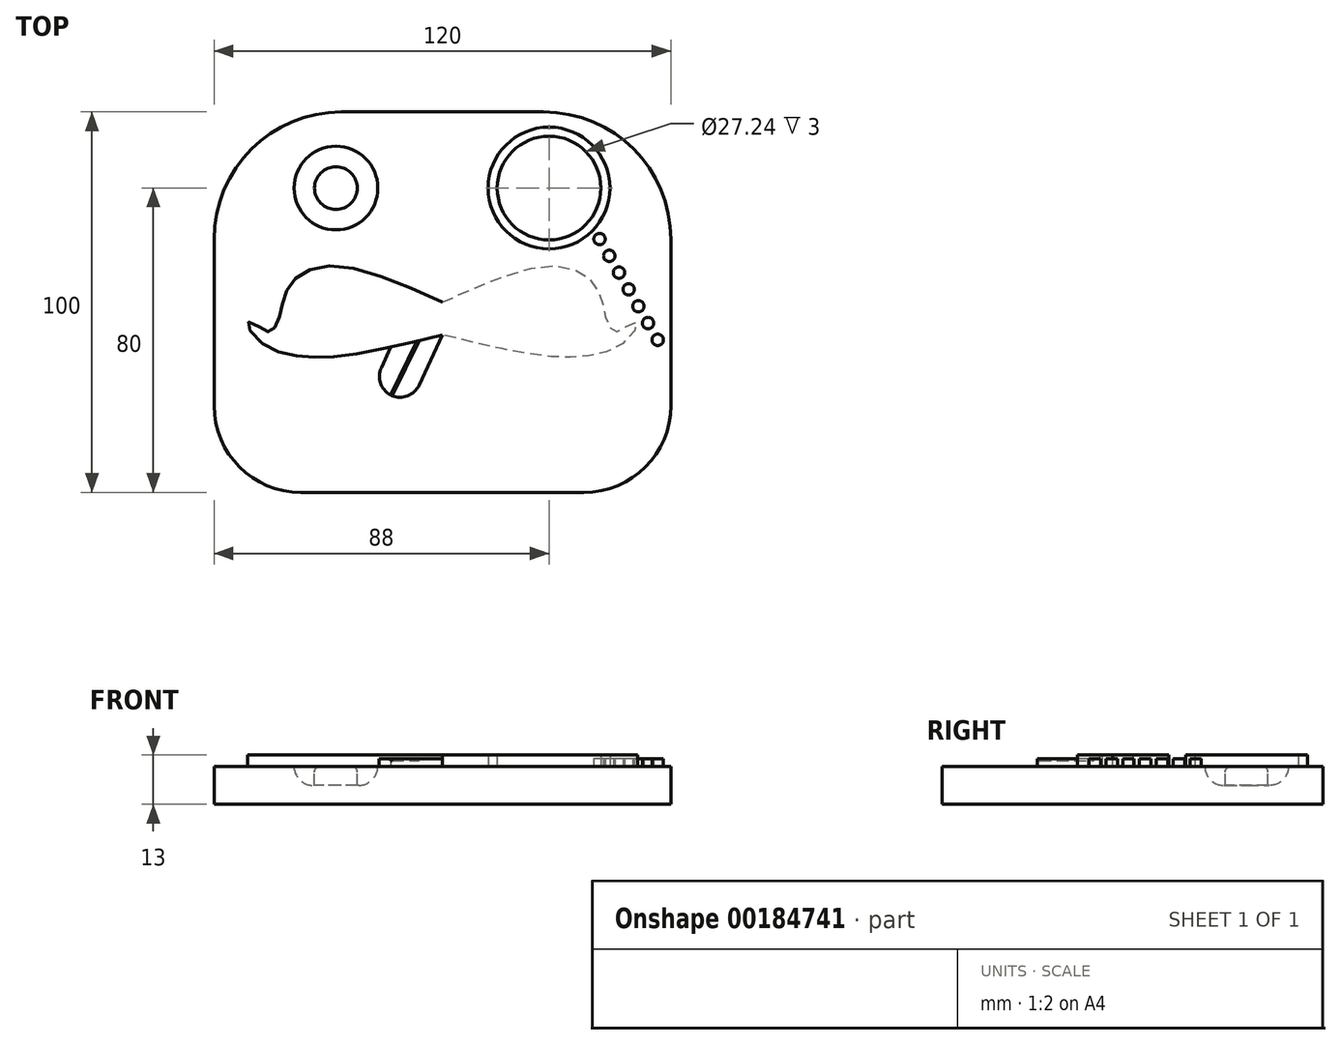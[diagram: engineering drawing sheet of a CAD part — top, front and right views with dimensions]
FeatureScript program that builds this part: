
annotation { "Feature Type Name" : "Feature", "Feature Type Description" : "" }
export const myFeature = defineFeature(function(context is Context, id is Id, definition is map)
    precondition{}
    {
        {
            var Q0;
            Q0=qCreatedBy(makeId("Top.planeOp"),FACE);
            var sketch = newSketch(context, id + "F0", { "sketchPlane" : qUnion([Q0])});
            skLineSegment(sketch, "E0.bottom", {"start": v(37.2, -50) * mm, "end": v(-37.2, -50) * mm});
            skLineSegment(sketch, "E0.top", {"start": v(26.57, 50) * mm, "end": v(-26.57, 50) * mm});
            skLineSegment(sketch, "E0.left", {"start": v(60, -27.2) * mm, "end": v(60, 16.57) * mm});
            skLineSegment(sketch, "E0.right", {"start": v(-60, -27.2) * mm, "end": v(-60, 16.57) * mm});
            skPoint(sketch, "E0.middle", {"position": v(0, 0) * mm});
            skPoint(sketch, "E1.visualSharp", {"position": v(-60, 50) * mm});
            skArc(sketch, "E1.filletArc", {"start": v(-26.57, 50) * mm, "mid": v(-50.2, 40.2) * mm, "end": v(-60, 16.57) * mm});
            skPoint(sketch, "E2.visualSharp", {"position": v(60, 50) * mm});
            skArc(sketch, "E2.filletArc", {"start": v(60, 16.57) * mm, "mid": v(50.2, 40.2) * mm, "end": v(26.57, 50) * mm});
            skPoint(sketch, "E3.visualSharp", {"position": v(-60, -50) * mm});
            skArc(sketch, "E3.filletArc", {"start": v(-60, -27.2) * mm, "mid": v(-53.32, -43.32) * mm, "end": v(-37.2, -50) * mm});
            skPoint(sketch, "E4.visualSharp", {"position": v(60, -50) * mm});
            skArc(sketch, "E4.filletArc", {"start": v(37.2, -50) * mm, "mid": v(53.32, -43.32) * mm, "end": v(60, -27.2) * mm});
            skSolve(sketch);
        }
        {
            var Q0;
            Q0 = qSketchRegion(id + "F0", true);
            extrude(context, id + "F1", {"entities" : qUnion([Q0]), "depth" : 10 * mm});
        }
        {
            var Q0;
            Q0=makeQuery(id+"F1.opExtrude","CAP_FACE",FACE,{"disambiguationData":[OSD([sQuery(id+"F0.wireOp",EDGE,"E0.bottom"),sQuery(id+"F0.wireOp",EDGE,"E0.top"),sQuery(id+"F0.wireOp",EDGE,"E0.left"),sQuery(id+"F0.wireOp",EDGE,"E0.right"),sQuery(id+"F0.wireOp",EDGE,"E1.filletArc"),sQuery(id+"F0.wireOp",EDGE,"E2.filletArc"),sQuery(id+"F0.wireOp",EDGE,"E3.filletArc"),sQuery(id+"F0.wireOp",EDGE,"E4.filletArc")])],"isStart":false});
            cPlane(context, id + "F2", {"entities" : qUnion([Q0]), "cplaneType" : CPlaneType.OFFSET, "offset" : 0 * mm, "width" : 150 * mm, "height" : 150 * mm});
        }
        {
            var Q0;
            Q0=qCreatedBy(id+"F2.planeOp",FACE);
            var sketch = newSketch(context, id + "F3", { "sketchPlane" : qUnion([Q0])});
            skFitSpline(sketch, "E5", {"points": [v(0, 0) * mm, v(-28.4, 9.57) * mm, v(-38.75, 6) * mm, v(-41.96, 0) * mm, v(-43.27, -5.29) * mm, v(-45.4, -7.79) * mm, v(-47.3, -6.95) * mm, v(-51.11, -5.29) * mm, v(-48.14, -10.28) * mm, v(-38.28, -14.09) * mm, v(-26.03, -14.09) * mm, v(0, -8.62) * mm], "startDerivative": vector(-190.26, 85.43) * mm, "endDerivative": vector(183.95, 44.61) * mm});
            skLineSegment(sketch, "E6", {"start": v(0, 71.97) * mm, "end": v(0, -72.57) * mm, "construction": true});
            skFitSpline(sketch, "E7.MirrorCS", {"points": [v(0, 0) * mm, v(28.4, 9.57) * mm, v(38.75, 6) * mm, v(41.96, 0) * mm, v(43.27, -5.29) * mm, v(45.4, -7.79) * mm, v(47.3, -6.95) * mm, v(51.11, -5.29) * mm, v(48.14, -10.28) * mm, v(38.28, -14.09) * mm, v(26.03, -14.09) * mm, v(0, -8.62) * mm], "startDerivative": vector(190.26, 85.43) * mm, "endDerivative": vector(-183.95, 44.61) * mm});
            skSolve(sketch);
        }
        {
            var Q0;
            Q0 = qSketchRegion(id + "F3", true);
            extrude(context, id + "F4", {"entities" : qUnion([Q0]), "operationType" : NewBodyOperationType.ADD, "depth" : 3 * mm});
        }
        {
            var Q0;
            Q0=qCreatedBy(id+"F2.planeOp",FACE);
            var sketch = newSketch(context, id + "F5", { "sketchPlane" : qUnion([Q0])});
            skLineSegment(sketch, "E8.bottom", {"start": v(-9.75, -3.6) * mm, "end": v(0.16, -8.23) * mm});
            skLineSegment(sketch, "E8.left", {"start": v(-9.75, -3.6) * mm, "end": v(-16.09, -17.2) * mm});
            skLineSegment(sketch, "E8.right", {"start": v(0.16, -8.23) * mm, "end": v(-6.18, -21.82) * mm});
            skLineSegment(sketch, "E9", {"start": v(0, 74.11) * mm, "end": v(0, -72.57) * mm, "construction": true});
            skArc(sketch, "E10", {"start": v(-16.09, -17.2) * mm, "mid": v(-13.44, -24.47) * mm, "end": v(-6.18, -21.82) * mm});
            skSolve(sketch);
        }
        {
            var Q0;
            Q0 = qSketchRegion(id + "F5", true);
            extrude(context, id + "F6", {"entities" : qUnion([Q0]), "operationType" : NewBodyOperationType.ADD, "depth" : 2 * mm});
        }
        {
            var Q0;
            Q0=qCreatedBy(id+"F2.planeOp",FACE);
            var sketch = newSketch(context, id + "F7", { "sketchPlane" : qUnion([Q0])});
            skLineSegment(sketch, "E11", {"start": v(0, 80.6) * mm, "end": v(0, -78.54) * mm, "construction": true});
            skCircle(sketch, "E12", {"center": v(-28, 30) * mm, "radius": 11 * mm});
            skCircle(sketch, "E13", {"center": v(-28, 30) * mm, "radius": 5.62 * mm});
            skCircle(sketch, "E14.MirrorC", {"center": v(28, 30) * mm, "radius": 11 * mm});
            skCircle(sketch, "E15.MirrorC", {"center": v(28, 30) * mm, "radius": 5.62 * mm});
            skSolve(sketch);
        }
        {
            var Q0;
            Q0=makeQuery(id+"F7.imprint","IMPRINT",FACE,{"disambiguationData":[TD([[makeQuery(id+"F7.imprint","IMPRINT",EDGE,{"derivedFrom":sQuery(id+"F7.wireOp",EDGE,"E12")}),1.0]])]});
            var Q1;
            Q1=makeQuery(id+"F7.imprint","IMPRINT",FACE,{"disambiguationData":[TD([[makeQuery(id+"F7.imprint","IMPRINT",EDGE,{"derivedFrom":sQuery(id+"F7.wireOp",EDGE,"E14.MirrorC")}),-1.0]])]});
            var Q2;
            Q2=sQuery(id+"F7.wireOp",EDGE,"E12");
            extrude(context, id + "F8", {"entities" : qUnion([Q0, Q1]), "operationType" : NewBodyOperationType.REMOVE, "surfaceEntities" : qUnion([Q2]), "oppositeDirection" : true, "depth" : 5 * mm});
        }
        {
            var Q0;
            Q0=makeQuery(id+"F8.boolean.opBoolean","COPY",EDGE,{"derivedFrom":makeQuery(id+"F8.opExtrude","CAP_EDGE",EDGE,{"disambiguationData":[OSD([sQuery(id+"F7.wireOp",EDGE,"E12")])],"isStart":false})});
            var Q1;
            Q1=makeQuery(id+"F8.boolean.opBoolean","COPY",EDGE,{"derivedFrom":makeQuery(id+"F8.opExtrude","CAP_EDGE",EDGE,{"disambiguationData":[OSD([sQuery(id+"F7.wireOp",EDGE,"E14.MirrorC")])],"isStart":false})});
            fillet(context, id + "F9", {"entities" : qUnion([Q0, Q1]), "radius" : 5 * mm, "tangentPropagation" : true, "allowEdgeOverflow" : false});
        }
        {
            var Q0;
            Q0=makeQuery(id+"F8.boolean.opBoolean","COPY",EDGE,{"derivedFrom":makeQuery(id+"F8.opExtrude","CAP_EDGE",EDGE,{"disambiguationData":[OSD([sQuery(id+"F7.wireOp",EDGE,"E13")])],"isStart":true})});
            var Q1;
            Q1=makeQuery(id+"F8.boolean.opBoolean","COPY",EDGE,{"derivedFrom":makeQuery(id+"F8.opExtrude","CAP_EDGE",EDGE,{"disambiguationData":[OSD([sQuery(id+"F7.wireOp",EDGE,"E15.MirrorC")])],"isStart":true})});
            fillet(context, id + "F10", {"entities" : qUnion([Q0, Q1]), "radius" : 1.5 * mm, "tangentPropagation" : true, "allowEdgeOverflow" : false});
        }
        {
            var Q0;
            Q0=qCreatedBy(id+"F2.planeOp",FACE);
            var sketch = newSketch(context, id + "F11", { "sketchPlane" : qUnion([Q0])});
            skCircle(sketch, "E16", {"center": v(28, 30) * mm, "radius": 13.62 * mm});
            skCircle(sketch, "E17", {"center": v(28, 30) * mm, "radius": 16 * mm});
            skSolve(sketch);
        }
        {
            var Q0;
            Q0=makeQuery(id+"F11.imprint","IMPRINT",FACE,{"disambiguationData":[TD([[makeQuery(id+"F11.imprint","IMPRINT",EDGE,{"derivedFrom":sQuery(id+"F11.wireOp",EDGE,"E16")}),-1.0]])]});
            extrude(context, id + "F12", {"entities" : qUnion([Q0]), "operationType" : NewBodyOperationType.ADD, "depth" : 3 * mm});
        }
        {
            var Q0;
            Q0=qCreatedBy(id+"F2.planeOp",FACE);
            var sketch = newSketch(context, id + "F13", { "sketchPlane" : qUnion([Q0])});
            skCircle(sketch, "E18", {"center": v(41.27, 16.6) * mm, "radius": 1.5 * mm});
            skCircle(sketch, "E19.0.1.0", {"center": v(43.82, 12.18) * mm, "radius": 1.5 * mm});
            skCircle(sketch, "E19.0.2.0", {"center": v(46.37, 7.76) * mm, "radius": 1.5 * mm});
            skCircle(sketch, "E19.0.3.0", {"center": v(48.92, 3.35) * mm, "radius": 1.5 * mm});
            skCircle(sketch, "E19.0.4.0", {"center": v(51.47, -1.07) * mm, "radius": 1.5 * mm});
            skLineSegment(sketch, "E19.direction1", {"start": v(41.27, 16.6) * mm, "end": v(57.63, 16.6) * mm, "construction": true});
            skLineSegment(sketch, "E19.direction2", {"start": v(41.27, 16.6) * mm, "end": v(43.82, 12.18) * mm, "construction": true});
            skCircle(sketch, "E20.0.0.5", {"center": v(54.02, -5.49) * mm, "radius": 1.5 * mm});
            skCircle(sketch, "E20.0.0.6", {"center": v(56.57, -9.9) * mm, "radius": 1.5 * mm});
            skSolve(sketch);
        }
        {
            var Q0;
            Q0 = qSketchRegion(id + "F13", true);
            var Q1;
            Q1 = qConstructionFilter(qBodyType(qCreatedBy(id + "F13" ,EDGE), BodyType.WIRE), ConstructionObject.NO);
            extrude(context, id + "F14", {"entities" : qUnion([Q0]), "operationType" : NewBodyOperationType.ADD, "surfaceEntities" : qUnion([Q1]), "depth" : 2 * mm});
        }
        {
            var Q0;
            Q0=makeQuery(id+"F6.opExtrude","CAP_FACE",FACE,{"disambiguationData":[OSD([sQuery(id+"F5.wireOp",EDGE,"E8.bottom"),sQuery(id+"F5.wireOp",EDGE,"E8.left"),sQuery(id+"F5.wireOp",EDGE,"E8.right"),sQuery(id+"F5.wireOp",EDGE,"E10")])],"isStart":false});
            var sketch = newSketch(context, id + "F15", { "sketchPlane" : qUnion([Q0])});
            skLineSegment(sketch, "E21", {"start": v(-13.44, -24.47) * mm, "end": v(-6.5, -10.18) * mm});
            skLineSegment(sketch, "E22", {"start": v(-13.21, -24.57) * mm, "end": v(-6.18, -10.1) * mm});
            skLineSegment(sketch, "E23", {"start": v(-13.67, -24.36) * mm, "end": v(-6.8, -10.26) * mm});
            skSolve(sketch);
        }
        {
            var Q0;
            {var subQ0=sQuery(id+"F15.wireOp",EDGE,"E21");Q0=makeQuery(id+"F15.imprint","IMPRINT",FACE,{"disambiguationData":[TD([[makeQuery(id+"F15.imprint","IMPRINT",EDGE,{"derivedFrom":subQ0}),1.0]])]});}
            var Q1;
            {var subQ0=sQuery(id+"F15.wireOp",EDGE,"E21");Q1=makeQuery(id+"F15.imprint","IMPRINT",FACE,{"disambiguationData":[TD([[makeQuery(id+"F15.imprint","IMPRINT",EDGE,{"derivedFrom":subQ0}),-1.0]])]});}
            extrude(context, id + "F16", {"entities" : qUnion([Q0, Q1]), "operationType" : NewBodyOperationType.REMOVE, "oppositeDirection" : true, "depth" : .5 * mm});
        }
    });
